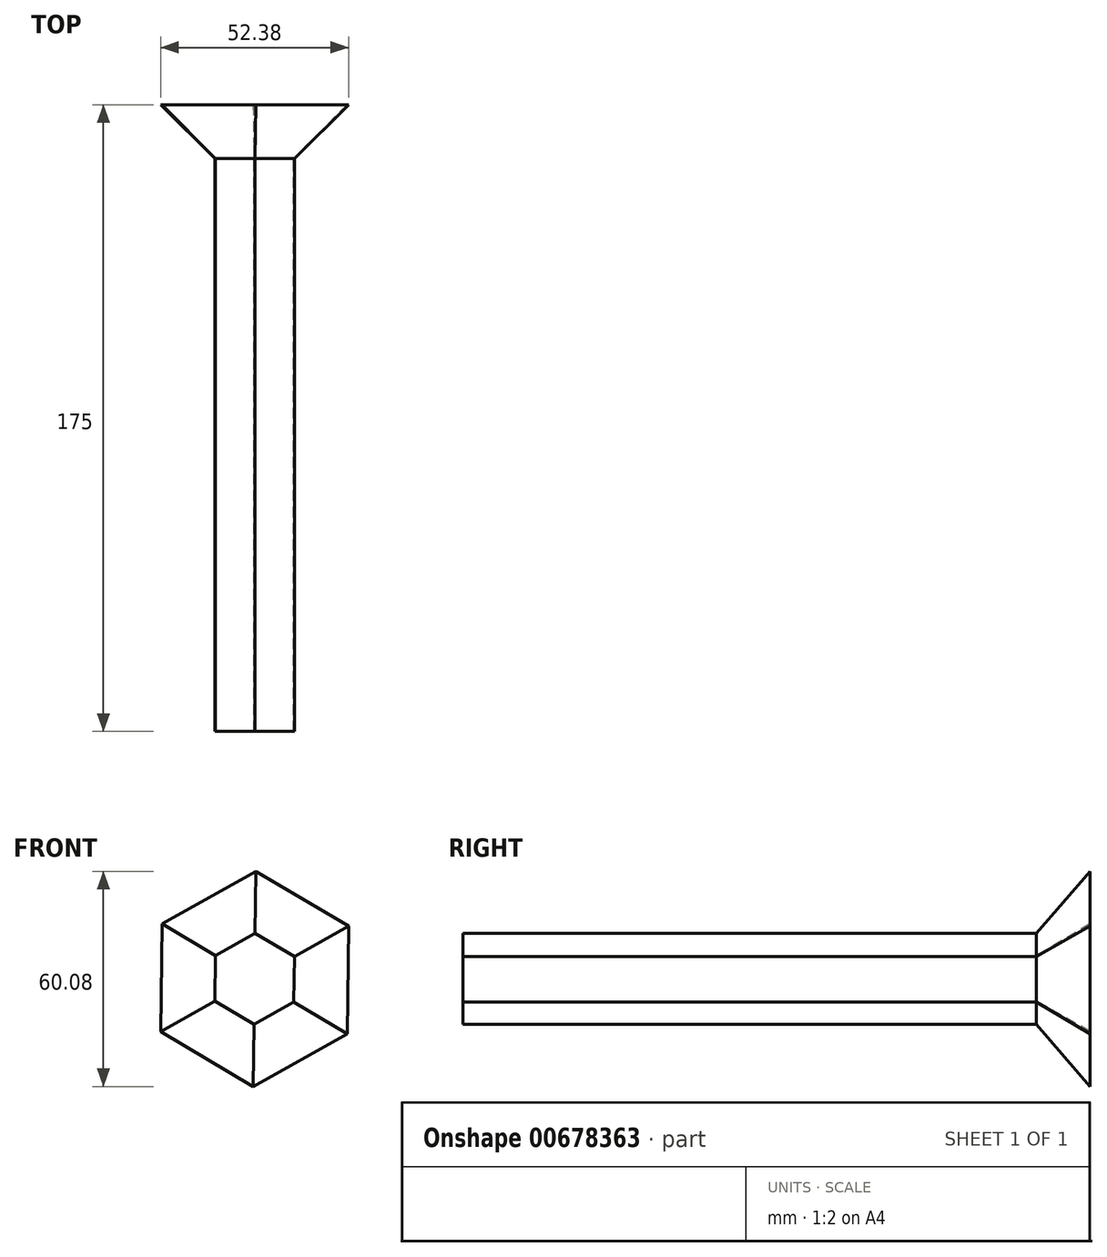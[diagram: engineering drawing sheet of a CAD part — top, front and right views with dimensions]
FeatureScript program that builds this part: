
annotation { "Feature Type Name" : "Feature", "Feature Type Description" : "" }
export const myFeature = defineFeature(function(context is Context, id is Id, definition is map)
    precondition{}
    {
        {
            var Q0;
            Q0=qCreatedBy(makeId("Front.planeOp"),FACE);
            var sketch = newSketch(context, id + "F0", { "sketchPlane" : qUnion([Q0])});
            skCircle(sketch, "E0.cCircle", {"center": v(0, 0) * mm, "radius": 11.02 * mm, "construction": true});
            skLineSegment(sketch, "E0.0", {"start": v(-0.15, -12.72) * mm, "end": v(-11.1, -6.23) * mm});
            skLineSegment(sketch, "E0.1", {"start": v(-11.1, -6.23) * mm, "end": v(-10.94, 6.5) * mm});
            skLineSegment(sketch, "E0.2", {"start": v(-10.94, 6.5) * mm, "end": v(0.15, 12.72) * mm});
            skLineSegment(sketch, "E0.3", {"start": v(0.15, 12.72) * mm, "end": v(11.1, 6.23) * mm});
            skLineSegment(sketch, "E0.4", {"start": v(11.1, 6.23) * mm, "end": v(10.94, -6.5) * mm});
            skLineSegment(sketch, "E0.5", {"start": v(10.94, -6.5) * mm, "end": v(-0.15, -12.72) * mm});
            skSolve(sketch);
        }
        {
            var Q0;
            Q0=makeQuery(id+"F0.imprint","IMPRINT",FACE,{"disambiguationData":[TD([[makeQuery(id+"F0.imprint","IMPRINT",EDGE,{"derivedFrom":sQuery(id+"F0.wireOp",EDGE,"E0.0")}),-1.0]])]});
            extrude(context, id + "F1", {"entities" : qUnion([Q0]), "depth" : 160 * mm, "offsetDistance" : 25 * mm});
        }
        {
            var Q0;
            Q0=makeQuery(id+"F1.opExtrude","CAP_FACE",FACE,{"disambiguationData":[OSD([sQuery(id+"F0.wireOp",EDGE,"E0.0"),sQuery(id+"F0.wireOp",EDGE,"E0.1"),sQuery(id+"F0.wireOp",EDGE,"E0.2"),sQuery(id+"F0.wireOp",EDGE,"E0.3"),sQuery(id+"F0.wireOp",EDGE,"E0.4"),sQuery(id+"F0.wireOp",EDGE,"E0.5")])],"isStart":true});
            extrude(context, id + "F2", {"entities" : qUnion([Q0]), "operationType" : NewBodyOperationType.ADD, "depth" : 15 * mm, "offsetDistance" : 25 * mm, "hasDraft" : true, "draftAngle" : 45 * degree});
        }
    });
